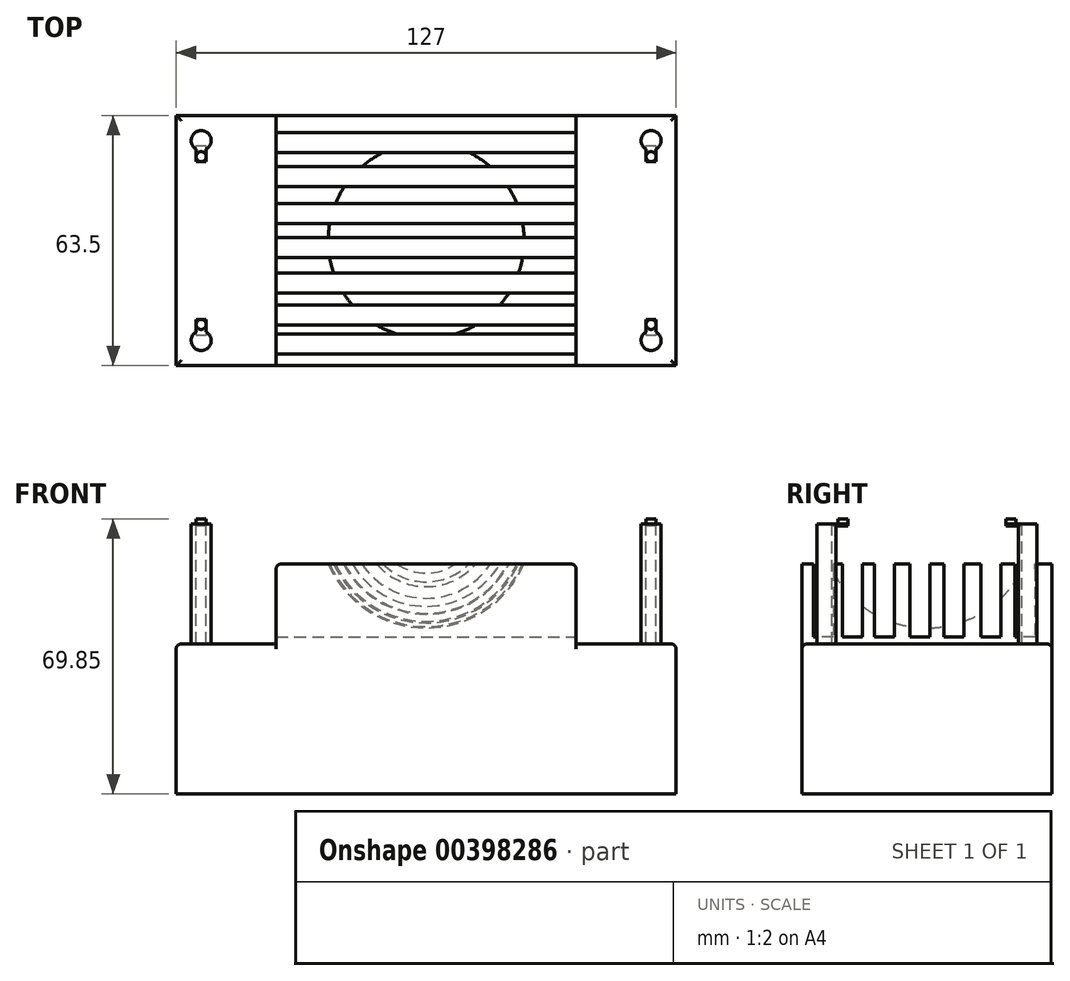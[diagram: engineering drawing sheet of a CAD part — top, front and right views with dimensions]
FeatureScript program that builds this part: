
annotation { "Feature Type Name" : "Feature", "Feature Type Description" : "" }
export const myFeature = defineFeature(function(context is Context, id is Id, definition is map)
    precondition{}
    {
        {
            var Q0;
            Q0=qCreatedBy(makeId("Top.planeOp"),FACE);
            var sketch = newSketch(context, id + "F0", { "sketchPlane" : qUnion([Q0])});
            skLineSegment(sketch, "E0.bottom", {"start": v(63.5, -31.75) * mm, "end": v(-63.5, -31.75) * mm});
            skLineSegment(sketch, "E0.top", {"start": v(63.5, 31.75) * mm, "end": v(-63.5, 31.75) * mm});
            skLineSegment(sketch, "E0.left", {"start": v(63.5, -31.75) * mm, "end": v(63.5, 31.75) * mm});
            skLineSegment(sketch, "E0.right", {"start": v(-63.5, -31.75) * mm, "end": v(-63.5, 31.75) * mm});
            skPoint(sketch, "E0.middle", {"position": v(0, 0) * mm});
            skSolve(sketch);
        }
        {
            var Q0;
            Q0=makeQuery(id+"F0.imprint","IMPRINT",FACE,{"disambiguationData":[TD([[makeQuery(id+"F0.imprint","IMPRINT",EDGE,{"derivedFrom":sQuery(id+"F0.wireOp",EDGE,"E0.bottom")}),-1.0]])]});
            extrude(context, id + "F1", {"entities" : qUnion([Q0]), "depth" : 38.1 * mm});
        }
        {
            var Q0;
            Q0=makeQuery(id+"F1.opExtrude","CAP_FACE",FACE,{"disambiguationData":[OSD([sQuery(id+"F0.wireOp",EDGE,"E0.bottom"),sQuery(id+"F0.wireOp",EDGE,"E0.top"),sQuery(id+"F0.wireOp",EDGE,"E0.left"),sQuery(id+"F0.wireOp",EDGE,"E0.right")])],"isStart":false});
            var sketch = newSketch(context, id + "F2", { "sketchPlane" : qUnion([Q0])});
            skLineSegment(sketch, "E1.bottom", {"start": v(-38.1, 31.75) * mm, "end": v(38.1, 31.75) * mm});
            skLineSegment(sketch, "E1.top", {"start": v(-38.1, -31.75) * mm, "end": v(38.1, -31.75) * mm});
            skLineSegment(sketch, "E1.left", {"start": v(-38.1, 31.75) * mm, "end": v(-38.1, -31.75) * mm});
            skLineSegment(sketch, "E1.right", {"start": v(38.1, 31.75) * mm, "end": v(38.1, -31.75) * mm});
            skSolve(sketch);
        }
        {
            var Q0;
            Q0=makeQuery(id+"F2.imprint","IMPRINT",FACE,{"disambiguationData":[TD([[makeQuery(id+"F2.imprint","IMPRINT",EDGE,{"derivedFrom":sQuery(id+"F2.wireOp",EDGE,"E1.bottom")}),1.0]])]});
            extrude(context, id + "F3", {"entities" : qUnion([Q0]), "operationType" : NewBodyOperationType.ADD, "depth" : 20.32 * mm});
        }
        {
            var Q0;
            Q0=qCreatedBy(makeId("Top.planeOp"),FACE);
            cPlane(context, id + "F4", {"entities" : qUnion([Q0]), "cplaneType" : CPlaneType.OFFSET, "offset" : 74.68 * mm, "width" : 152.4 * mm, "height" : 152.4 * mm});
        }
        {
            var Q0;
            Q0=qCreatedBy(id+"F4.planeOp",FACE);
            var sketch = newSketch(context, id + "F5", { "sketchPlane" : qUnion([Q0])});
            skLineSegment(sketch, "E2.bottom", {"start": v(-41.41, 27.43) * mm, "end": v(44.52, 27.43) * mm});
            skLineSegment(sketch, "E2.top", {"start": v(-41.41, 22.35) * mm, "end": v(44.52, 22.35) * mm});
            skLineSegment(sketch, "E2.left", {"start": v(-41.41, 27.43) * mm, "end": v(-41.41, 22.35) * mm});
            skLineSegment(sketch, "E2.right", {"start": v(44.52, 27.43) * mm, "end": v(44.52, 22.35) * mm});
            skLineSegment(sketch, "E3.bottom", {"start": v(-41.03, 18.8) * mm, "end": v(44.9, 18.8) * mm});
            skLineSegment(sketch, "E3.top", {"start": v(-41.03, 13.72) * mm, "end": v(44.9, 13.72) * mm});
            skLineSegment(sketch, "E3.left", {"start": v(-41.03, 18.8) * mm, "end": v(-41.03, 13.72) * mm});
            skLineSegment(sketch, "E3.right", {"start": v(44.9, 18.8) * mm, "end": v(44.9, 13.72) * mm});
            skLineSegment(sketch, "E4.bottom", {"start": v(-41, 9.4) * mm, "end": v(44.94, 9.4) * mm});
            skLineSegment(sketch, "E4.top", {"start": v(-41, 4.32) * mm, "end": v(44.94, 4.32) * mm});
            skLineSegment(sketch, "E4.left", {"start": v(-41, 9.4) * mm, "end": v(-41, 4.32) * mm});
            skLineSegment(sketch, "E4.right", {"start": v(44.94, 9.4) * mm, "end": v(44.94, 4.32) * mm});
            skLineSegment(sketch, "E5.bottom", {"start": v(-40.8, 0.73) * mm, "end": v(45.13, 0.73) * mm});
            skLineSegment(sketch, "E5.top", {"start": v(-40.8, -4.35) * mm, "end": v(45.13, -4.35) * mm});
            skLineSegment(sketch, "E5.left", {"start": v(-40.8, 0.73) * mm, "end": v(-40.8, -4.35) * mm});
            skLineSegment(sketch, "E5.right", {"start": v(45.13, 0.73) * mm, "end": v(45.13, -4.35) * mm});
            skLineSegment(sketch, "E6.bottom", {"start": v(-40.2, -8.25) * mm, "end": v(45.73, -8.25) * mm});
            skLineSegment(sketch, "E6.top", {"start": v(-40.2, -13.33) * mm, "end": v(45.73, -13.33) * mm});
            skLineSegment(sketch, "E6.left", {"start": v(-40.2, -8.25) * mm, "end": v(-40.2, -13.33) * mm});
            skLineSegment(sketch, "E6.right", {"start": v(45.73, -8.25) * mm, "end": v(45.73, -13.33) * mm});
            skLineSegment(sketch, "E7.bottom", {"start": v(-40.68, -16.38) * mm, "end": v(45.25, -16.38) * mm});
            skLineSegment(sketch, "E7.top", {"start": v(-40.68, -21.46) * mm, "end": v(45.25, -21.46) * mm});
            skLineSegment(sketch, "E7.left", {"start": v(-40.68, -16.38) * mm, "end": v(-40.68, -21.46) * mm});
            skLineSegment(sketch, "E7.right", {"start": v(45.25, -16.38) * mm, "end": v(45.25, -21.46) * mm});
            skLineSegment(sketch, "E8.bottom", {"start": v(-40.56, -23.75) * mm, "end": v(45.38, -23.75) * mm});
            skLineSegment(sketch, "E8.top", {"start": v(-40.56, -28.83) * mm, "end": v(45.38, -28.83) * mm});
            skLineSegment(sketch, "E8.left", {"start": v(-40.56, -23.75) * mm, "end": v(-40.56, -28.83) * mm});
            skLineSegment(sketch, "E8.right", {"start": v(45.38, -23.75) * mm, "end": v(45.38, -28.83) * mm});
            skSolve(sketch);
        }
        {
            var Q0;
            Q0 = qSketchRegion(id + "F5", true);
            extrude(context, id + "F6", {"entities" : qUnion([Q0]), "operationType" : NewBodyOperationType.REMOVE, "oppositeDirection" : true, "depth" : 34.8 * mm});
        }
        {
            var Q0;
            Q0=makeQuery(id+"F1.opExtrude","CAP_EDGE",EDGE,{"disambiguationData":[OSD([sQuery(id+"F0.wireOp",EDGE,"E0.right")])],"isStart":false});
            var Q1;
            {var subQ0=sQuery(id+"F0.wireOp",EDGE,"E0.right");var subQ1=sQuery(id+"F0.wireOp",EDGE,"E0.bottom");Q1=makeQuery(id+"F3.boolean.opBoolean","SPLIT",EDGE,{"disambiguationData":[TD([makeQuery(id+"F1.opExtrude","SWEPT_FACE",FACE,{"disambiguationData":[OSD([subQ0])]})])],"derivedFrom":makeQuery(id+"F1.opExtrude","CAP_EDGE",EDGE,{"disambiguationData":[OSD([subQ1])],"isStart":false})});}
            var Q2;
            {var subQ0=sQuery(id+"F2.wireOp",EDGE,"E1.left");Q2=makeQuery(id+"F6.boolean.opBoolean","SPLIT",EDGE,{"disambiguationData":[TD([makeQuery(id+"F6.opExtrude","SWEPT_FACE",FACE,{"disambiguationData":[OSD([sQuery(id+"F5.wireOp",EDGE,"E5.top")])]})])],"derivedFrom":makeQuery(id+"F3.opExtrude","CAP_EDGE",EDGE,{"disambiguationData":[OSD([subQ0])],"isStart":false})});}
            var Q3;
            {var subQ0=sQuery(id+"F2.wireOp",EDGE,"E1.left");Q3=makeQuery(id+"F6.boolean.opBoolean","SPLIT",EDGE,{"disambiguationData":[TD([makeQuery(id+"F6.opExtrude","SWEPT_FACE",FACE,{"disambiguationData":[OSD([sQuery(id+"F5.wireOp",EDGE,"E6.top")])]})])],"derivedFrom":makeQuery(id+"F3.opExtrude","CAP_EDGE",EDGE,{"disambiguationData":[OSD([subQ0])],"isStart":false})});}
            var Q4;
            {var subQ0=sQuery(id+"F2.wireOp",EDGE,"E1.left");Q4=makeQuery(id+"F6.boolean.opBoolean","SPLIT",EDGE,{"disambiguationData":[TD([makeQuery(id+"F1.opExtrude","SWEPT_FACE",FACE,{"disambiguationData":[OSD([sQuery(id+"F0.wireOp",EDGE,"E0.bottom")])]})])],"derivedFrom":makeQuery(id+"F3.opExtrude","CAP_EDGE",EDGE,{"disambiguationData":[OSD([subQ0])],"isStart":false})});}
            var Q5;
            {var subQ0=sQuery(id+"F2.wireOp",EDGE,"E1.left");Q5=makeQuery(id+"F6.boolean.opBoolean","SPLIT",EDGE,{"disambiguationData":[TD([makeQuery(id+"F6.opExtrude","SWEPT_FACE",FACE,{"disambiguationData":[OSD([sQuery(id+"F5.wireOp",EDGE,"E7.top")])]})])],"derivedFrom":makeQuery(id+"F3.opExtrude","CAP_EDGE",EDGE,{"disambiguationData":[OSD([subQ0])],"isStart":false})});}
            var Q6;
            {var subQ0=sQuery(id+"F2.wireOp",EDGE,"E1.left");Q6=makeQuery(id+"F6.boolean.opBoolean","SPLIT",EDGE,{"disambiguationData":[TD([makeQuery(id+"F6.opExtrude","SWEPT_FACE",FACE,{"disambiguationData":[OSD([sQuery(id+"F5.wireOp",EDGE,"E3.top")])]})])],"derivedFrom":makeQuery(id+"F3.opExtrude","CAP_EDGE",EDGE,{"disambiguationData":[OSD([subQ0])],"isStart":false})});}
            var Q7;
            {var subQ0=sQuery(id+"F2.wireOp",EDGE,"E1.left");Q7=makeQuery(id+"F6.boolean.opBoolean","SPLIT",EDGE,{"disambiguationData":[TD([makeQuery(id+"F6.opExtrude","SWEPT_FACE",FACE,{"disambiguationData":[OSD([sQuery(id+"F5.wireOp",EDGE,"E2.top")])]})])],"derivedFrom":makeQuery(id+"F3.opExtrude","CAP_EDGE",EDGE,{"disambiguationData":[OSD([subQ0])],"isStart":false})});}
            var Q8;
            {var subQ0=sQuery(id+"F2.wireOp",EDGE,"E1.left");Q8=makeQuery(id+"F6.boolean.opBoolean","SPLIT",EDGE,{"disambiguationData":[TD([makeQuery(id+"F1.opExtrude","SWEPT_FACE",FACE,{"disambiguationData":[OSD([sQuery(id+"F0.wireOp",EDGE,"E0.top")])]})])],"derivedFrom":makeQuery(id+"F3.opExtrude","CAP_EDGE",EDGE,{"disambiguationData":[OSD([subQ0])],"isStart":false})});}
            var Q9;
            {var subQ0=sQuery(id+"F2.wireOp",EDGE,"E1.left");Q9=makeQuery(id+"F6.boolean.opBoolean","SPLIT",EDGE,{"disambiguationData":[TD([makeQuery(id+"F6.opExtrude","SWEPT_FACE",FACE,{"disambiguationData":[OSD([sQuery(id+"F5.wireOp",EDGE,"E4.top")])]})])],"derivedFrom":makeQuery(id+"F3.opExtrude","CAP_EDGE",EDGE,{"disambiguationData":[OSD([subQ0])],"isStart":false})});}
            var Q10;
            {var subQ0=sQuery(id+"F0.wireOp",EDGE,"E0.right");var subQ1=sQuery(id+"F0.wireOp",EDGE,"E0.top");Q10=makeQuery(id+"F3.boolean.opBoolean","SPLIT",EDGE,{"disambiguationData":[TD([makeQuery(id+"F1.opExtrude","SWEPT_FACE",FACE,{"disambiguationData":[OSD([subQ0])]})])],"derivedFrom":makeQuery(id+"F1.opExtrude","CAP_EDGE",EDGE,{"disambiguationData":[OSD([subQ1])],"isStart":false})});}
            var Q11;
            Q11=makeQuery(id+"F1.opExtrude","CAP_EDGE",EDGE,{"disambiguationData":[OSD([sQuery(id+"F0.wireOp",EDGE,"E0.left")])],"isStart":false});
            var Q12;
            {var subQ0=sQuery(id+"F0.wireOp",EDGE,"E0.left");var subQ1=sQuery(id+"F0.wireOp",EDGE,"E0.top");Q12=makeQuery(id+"F3.boolean.opBoolean","SPLIT",EDGE,{"disambiguationData":[TD([makeQuery(id+"F1.opExtrude","SWEPT_FACE",FACE,{"disambiguationData":[OSD([subQ0])]})])],"derivedFrom":makeQuery(id+"F1.opExtrude","CAP_EDGE",EDGE,{"disambiguationData":[OSD([subQ1])],"isStart":false})});}
            var Q13;
            {var subQ0=sQuery(id+"F0.wireOp",EDGE,"E0.left");var subQ1=sQuery(id+"F0.wireOp",EDGE,"E0.bottom");Q13=makeQuery(id+"F3.boolean.opBoolean","SPLIT",EDGE,{"disambiguationData":[TD([makeQuery(id+"F1.opExtrude","SWEPT_FACE",FACE,{"disambiguationData":[OSD([subQ0])]})])],"derivedFrom":makeQuery(id+"F1.opExtrude","CAP_EDGE",EDGE,{"disambiguationData":[OSD([subQ1])],"isStart":false})});}
            var Q14;
            {var subQ0=sQuery(id+"F2.wireOp",EDGE,"E1.right");Q14=makeQuery(id+"F6.boolean.opBoolean","SPLIT",EDGE,{"disambiguationData":[TD([makeQuery(id+"F6.opExtrude","SWEPT_FACE",FACE,{"disambiguationData":[OSD([sQuery(id+"F5.wireOp",EDGE,"E4.top")])]})])],"derivedFrom":makeQuery(id+"F3.opExtrude","CAP_EDGE",EDGE,{"disambiguationData":[OSD([subQ0])],"isStart":false})});}
            var Q15;
            {var subQ0=sQuery(id+"F2.wireOp",EDGE,"E1.right");Q15=makeQuery(id+"F6.boolean.opBoolean","SPLIT",EDGE,{"disambiguationData":[TD([makeQuery(id+"F6.opExtrude","SWEPT_FACE",FACE,{"disambiguationData":[OSD([sQuery(id+"F5.wireOp",EDGE,"E3.top")])]})])],"derivedFrom":makeQuery(id+"F3.opExtrude","CAP_EDGE",EDGE,{"disambiguationData":[OSD([subQ0])],"isStart":false})});}
            var Q16;
            {var subQ0=sQuery(id+"F2.wireOp",EDGE,"E1.right");Q16=makeQuery(id+"F6.boolean.opBoolean","SPLIT",EDGE,{"disambiguationData":[TD([makeQuery(id+"F6.opExtrude","SWEPT_FACE",FACE,{"disambiguationData":[OSD([sQuery(id+"F5.wireOp",EDGE,"E2.top")])]})])],"derivedFrom":makeQuery(id+"F3.opExtrude","CAP_EDGE",EDGE,{"disambiguationData":[OSD([subQ0])],"isStart":false})});}
            var Q17;
            {var subQ0=sQuery(id+"F2.wireOp",EDGE,"E1.right");Q17=makeQuery(id+"F6.boolean.opBoolean","SPLIT",EDGE,{"disambiguationData":[TD([makeQuery(id+"F1.opExtrude","SWEPT_FACE",FACE,{"disambiguationData":[OSD([sQuery(id+"F0.wireOp",EDGE,"E0.top")])]})])],"derivedFrom":makeQuery(id+"F3.opExtrude","CAP_EDGE",EDGE,{"disambiguationData":[OSD([subQ0])],"isStart":false})});}
            var Q18;
            {var subQ0=sQuery(id+"F2.wireOp",EDGE,"E1.right");Q18=makeQuery(id+"F6.boolean.opBoolean","SPLIT",EDGE,{"disambiguationData":[TD([makeQuery(id+"F6.opExtrude","SWEPT_FACE",FACE,{"disambiguationData":[OSD([sQuery(id+"F5.wireOp",EDGE,"E5.top")])]})])],"derivedFrom":makeQuery(id+"F3.opExtrude","CAP_EDGE",EDGE,{"disambiguationData":[OSD([subQ0])],"isStart":false})});}
            var Q19;
            {var subQ0=sQuery(id+"F2.wireOp",EDGE,"E1.right");Q19=makeQuery(id+"F6.boolean.opBoolean","SPLIT",EDGE,{"disambiguationData":[TD([makeQuery(id+"F6.opExtrude","SWEPT_FACE",FACE,{"disambiguationData":[OSD([sQuery(id+"F5.wireOp",EDGE,"E6.top")])]})])],"derivedFrom":makeQuery(id+"F3.opExtrude","CAP_EDGE",EDGE,{"disambiguationData":[OSD([subQ0])],"isStart":false})});}
            var Q20;
            {var subQ0=sQuery(id+"F2.wireOp",EDGE,"E1.right");Q20=makeQuery(id+"F6.boolean.opBoolean","SPLIT",EDGE,{"disambiguationData":[TD([makeQuery(id+"F6.opExtrude","SWEPT_FACE",FACE,{"disambiguationData":[OSD([sQuery(id+"F5.wireOp",EDGE,"E7.top")])]})])],"derivedFrom":makeQuery(id+"F3.opExtrude","CAP_EDGE",EDGE,{"disambiguationData":[OSD([subQ0])],"isStart":false})});}
            var Q21;
            {var subQ0=sQuery(id+"F2.wireOp",EDGE,"E1.right");Q21=makeQuery(id+"F6.boolean.opBoolean","SPLIT",EDGE,{"disambiguationData":[TD([makeQuery(id+"F1.opExtrude","SWEPT_FACE",FACE,{"disambiguationData":[OSD([sQuery(id+"F0.wireOp",EDGE,"E0.bottom")])]})])],"derivedFrom":makeQuery(id+"F3.opExtrude","CAP_EDGE",EDGE,{"disambiguationData":[OSD([subQ0])],"isStart":false})});}
            fillet(context, id + "F7", {"entities" : qUnion([Q0, Q1, Q2, Q3, Q4, Q5, Q6, Q7, Q8, Q9, Q10, Q11, Q12, Q13, Q14, Q15, Q16, Q17, Q18, Q19, Q20, Q21]), "radius" : 1.27 * mm, "tangentPropagation" : true, "allowEdgeOverflow" : false});
        }
        {
            var Q0;
            Q0=qCreatedBy(makeId("Top.planeOp"),FACE);
            cPlane(context, id + "F8", {"entities" : qUnion([Q0]), "cplaneType" : CPlaneType.OFFSET, "offset" : 69.34 * mm, "width" : 152.4 * mm, "height" : 152.4 * mm});
        }
        {
            var Q0;
            Q0=qCreatedBy(id+"F8.planeOp",FACE);
            var sketch = newSketch(context, id + "F9", { "sketchPlane" : qUnion([Q0])});
            skCircle(sketch, "E9", {"center": v(0, 0) * mm, "radius": 27.18 * mm});
            skLineSegment(sketch, "E10", {"start": v(0, 27.18) * mm, "end": v(0, -27.18) * mm});
            skSolve(sketch);
        }
        {
            var Q0;
            Q0=qCreatedBy(id+"F8.planeOp",FACE);
            var sketch = newSketch(context, id + "F10", { "sketchPlane" : qUnion([Q0])});
            skLineSegment(sketch, "E11", {"start": v(0, 27.11) * mm, "end": v(0, -26.67) * mm});
            skSolve(sketch);
        }
        {
            var Q0;
            {var subQ0=sQuery(id+"F9.wireOp",EDGE,"E10");Q0=makeQuery(id+"F9.imprint","IMPRINT",FACE,{"disambiguationData":[TD([[makeQuery(id+"F9.imprint","IMPRINT",EDGE,{"derivedFrom":subQ0}),-1.0]])]});}
            var Q1;
            Q1=sQuery(id+"F10.wireOp",EDGE,"E11");
            revolve(context, id + "F11", {"operationType" : NewBodyOperationType.REMOVE, "entities" : qUnion([Q0]), "axis" : qUnion([Q1]), "revolveType" : RevolveType.FULL, "oppositeDirection" : true});
        }
        {
            var Q0;
            {var subQ0=sQuery(id+"F0.wireOp",EDGE,"E0.left");var subQ1=sQuery(id+"F0.wireOp",EDGE,"E0.top");var subQ2=sQuery(id+"F0.wireOp",EDGE,"E0.bottom");Q0=makeQuery(id+"F3.boolean.opBoolean","SPLIT",FACE,{"disambiguationData":[TD([makeQuery(id+"F1.opExtrude","SWEPT_FACE",FACE,{"disambiguationData":[OSD([subQ0])]})])],"derivedFrom":makeQuery(id+"F1.opExtrude","CAP_FACE",FACE,{"disambiguationData":[OSD([subQ2,subQ1,subQ0,sQuery(id+"F0.wireOp",EDGE,"E0.right")])],"isStart":false})});}
            var sketch = newSketch(context, id + "F12", { "sketchPlane" : qUnion([Q0])});
            skCircle(sketch, "E12", {"center": v(-57.15, 25.4) * mm, "radius": 2.54 * mm});
            skCircle(sketch, "E13", {"center": v(-57.15, -25.4) * mm, "radius": 2.54 * mm});
            skSolve(sketch);
        }
        {
            var Q0;
            Q0=makeQuery(id+"F12.imprint","IMPRINT",FACE,{"disambiguationData":[TD([[makeQuery(id+"F12.imprint","IMPRINT",EDGE,{"derivedFrom":sQuery(id+"F12.wireOp",EDGE,"E12")}),1.0]])]});
            var Q1;
            Q1=makeQuery(id+"F12.imprint","IMPRINT",FACE,{"disambiguationData":[TD([[makeQuery(id+"F12.imprint","IMPRINT",EDGE,{"derivedFrom":sQuery(id+"F12.wireOp",EDGE,"E13")}),1.0]])]});
            extrude(context, id + "F13", {"entities" : qUnion([Q0, Q1]), "operationType" : NewBodyOperationType.ADD, "depth" : 30.48 * mm});
        }
        {
            var Q0;
            {var subQ0=sQuery(id+"F0.wireOp",EDGE,"E0.left");var subQ1=sQuery(id+"F0.wireOp",EDGE,"E0.top");var subQ2=sQuery(id+"F0.wireOp",EDGE,"E0.bottom");Q0=makeQuery(id+"F3.boolean.opBoolean","SPLIT",FACE,{"disambiguationData":[TD([makeQuery(id+"F1.opExtrude","SWEPT_FACE",FACE,{"disambiguationData":[OSD([subQ0])]})])],"derivedFrom":makeQuery(id+"F1.opExtrude","CAP_FACE",FACE,{"disambiguationData":[OSD([subQ2,subQ1,subQ0,sQuery(id+"F0.wireOp",EDGE,"E0.right")])],"isStart":false})});}
            var sketch = newSketch(context, id + "F14", { "sketchPlane" : qUnion([Q0])});
            skCircle(sketch, "E14", {"center": v(57.15, 25.4) * mm, "radius": 2.54 * mm});
            skCircle(sketch, "E15", {"center": v(57.15, -25.4) * mm, "radius": 2.54 * mm});
            skSolve(sketch);
        }
        {
            var Q0;
            Q0=makeQuery(id+"F14.imprint","IMPRINT",FACE,{"disambiguationData":[TD([[makeQuery(id+"F14.imprint","IMPRINT",EDGE,{"derivedFrom":sQuery(id+"F14.wireOp",EDGE,"E14")}),1.0]])]});
            var Q1;
            Q1=makeQuery(id+"F14.imprint","IMPRINT",FACE,{"disambiguationData":[TD([[makeQuery(id+"F14.imprint","IMPRINT",EDGE,{"derivedFrom":sQuery(id+"F14.wireOp",EDGE,"E15")}),1.0]])]});
            extrude(context, id + "F15", {"entities" : qUnion([Q0, Q1]), "operationType" : NewBodyOperationType.ADD, "depth" : 30.48 * mm});
        }
        {
            var Q0;
            Q0=qCreatedBy(makeId("Top.planeOp"),FACE);
            cPlane(context, id + "F16", {"entities" : qUnion([Q0]), "cplaneType" : CPlaneType.OFFSET, "offset" : 68.83 * mm, "width" : 152.4 * mm, "height" : 152.4 * mm});
        }
        {
            var Q0;
            Q0=qCreatedBy(id+"F16.planeOp",FACE);
            var sketch = newSketch(context, id + "F17", { "sketchPlane" : qUnion([Q0])});
            skLineSegment(sketch, "E16.bottom", {"start": v(-58.42, 24.13) * mm, "end": v(-55.88, 24.13) * mm});
            skLineSegment(sketch, "E16.top", {"start": v(-58.42, -24.13) * mm, "end": v(-55.88, -24.13) * mm});
            skLineSegment(sketch, "E16.left", {"start": v(-58.42, 24.13) * mm, "end": v(-58.42, -24.13) * mm});
            skLineSegment(sketch, "E16.right", {"start": v(-55.88, 24.13) * mm, "end": v(-55.88, -24.13) * mm});
            skLineSegment(sketch, "E17.bottom", {"start": v(55.88, 24.13) * mm, "end": v(58.42, 24.13) * mm});
            skLineSegment(sketch, "E17.top", {"start": v(55.88, -24.13) * mm, "end": v(58.42, -24.13) * mm});
            skLineSegment(sketch, "E17.left", {"start": v(55.88, 24.13) * mm, "end": v(55.88, -24.13) * mm});
            skLineSegment(sketch, "E17.right", {"start": v(58.42, 24.13) * mm, "end": v(58.42, -24.13) * mm});
            skSolve(sketch);
        }
        {
            var Q0;
            Q0 = qSketchRegion(id + "F17", true);
            extrude(context, id + "F18", {"entities" : qUnion([Q0]), "operationType" : NewBodyOperationType.REMOVE, "oppositeDirection" : true, "depth" : 30.73 * mm});
        }
        {
            var Q0;
            Q0=makeQuery(id+"F18.boolean.opBoolean","COPY",FACE,{"derivedFrom":makeQuery(id+"F18.opExtrude","SWEPT_FACE",FACE,{"disambiguationData":[OSD([sQuery(id+"F17.wireOp",EDGE,"E16.bottom")])]})});
            var sketch = newSketch(context, id + "F19", { "sketchPlane" : qUnion([Q0])});
            skLineSegment(sketch, "E18.bottom", {"start": v(-58.42, 68.58) * mm, "end": v(-55.88, 68.58) * mm});
            skLineSegment(sketch, "E18.top", {"start": v(-58.42, 68.07) * mm, "end": v(-55.88, 68.07) * mm});
            skLineSegment(sketch, "E18.left", {"start": v(-58.42, 68.58) * mm, "end": v(-58.42, 68.07) * mm});
            skLineSegment(sketch, "E18.right", {"start": v(-55.88, 68.58) * mm, "end": v(-55.88, 68.07) * mm});
            skSolve(sketch);
        }
        {
            var Q0;
            Q0 = qSketchRegion(id + "F19", true);
            extrude(context, id + "F20", {"entities" : qUnion([Q0]), "operationType" : NewBodyOperationType.ADD, "depth" : 4.1 * mm});
        }
        {
            var Q0;
            Q0=makeQuery(id+"F20.boolean.opBoolean","MERGE",FACE,{"derivedFrom":[makeQuery(id+"F13.opExtrude","CAP_FACE",FACE,{"disambiguationData":[OSD([sQuery(id+"F12.wireOp",EDGE,"E12")])],"isStart":false}),makeQuery(id+"F20.opExtrude","SWEPT_FACE",FACE,{"disambiguationData":[OSD([sQuery(id+"F19.wireOp",EDGE,"E18.bottom")])]})]});
            var sketch = newSketch(context, id + "F21", { "sketchPlane" : qUnion([Q0])});
            skCircle(sketch, "E19", {"center": v(-57.15, 21.31) * mm, "radius": 1.27 * mm});
            skSolve(sketch);
        }
        {
            var Q0;
            Q0 = qSketchRegion(id + "F21", true);
            extrude(context, id + "F22", {"entities" : qUnion([Q0]), "operationType" : NewBodyOperationType.ADD, "depth" : 1.27 * mm});
        }
        {
            var Q0;
            Q0=makeQuery(id+"F18.boolean.opBoolean","COPY",FACE,{"derivedFrom":makeQuery(id+"F18.opExtrude","SWEPT_FACE",FACE,{"disambiguationData":[OSD([sQuery(id+"F17.wireOp",EDGE,"E16.top")])]})});
            var sketch = newSketch(context, id + "F23", { "sketchPlane" : qUnion([Q0])});
            skLineSegment(sketch, "E20.bottom", {"start": v(55.88, 68.58) * mm, "end": v(58.42, 68.58) * mm});
            skLineSegment(sketch, "E20.top", {"start": v(55.88, 68.07) * mm, "end": v(58.42, 68.07) * mm});
            skLineSegment(sketch, "E20.left", {"start": v(55.88, 68.58) * mm, "end": v(55.88, 68.07) * mm});
            skLineSegment(sketch, "E20.right", {"start": v(58.42, 68.58) * mm, "end": v(58.42, 68.07) * mm});
            skSolve(sketch);
        }
        {
            var Q0;
            Q0 = qSketchRegion(id + "F23", true);
            extrude(context, id + "F24", {"entities" : qUnion([Q0]), "operationType" : NewBodyOperationType.ADD, "depth" : 4.1 * mm});
        }
        {
            var Q0;
            Q0=makeQuery(id+"F24.boolean.opBoolean","MERGE",FACE,{"derivedFrom":[makeQuery(id+"F13.opExtrude","CAP_FACE",FACE,{"disambiguationData":[OSD([sQuery(id+"F12.wireOp",EDGE,"E13")])],"isStart":false}),makeQuery(id+"F24.opExtrude","SWEPT_FACE",FACE,{"disambiguationData":[OSD([sQuery(id+"F23.wireOp",EDGE,"E20.bottom")])]})]});
            var sketch = newSketch(context, id + "F25", { "sketchPlane" : qUnion([Q0])});
            skCircle(sketch, "E21", {"center": v(-57.15, -21.31) * mm, "radius": 1.27 * mm});
            skSolve(sketch);
        }
        {
            var Q0;
            {var subQ0=sQuery(id+"F25.wireOp",EDGE,"E21");var subQ1=sQuery(id+"F23.wireOp",EDGE,"E20.bottom");var subQ2=makeQuery(id+"F25.imprint","INTERSECT",VERTEX,{"derivedFrom":[makeQuery(id+"F24.opExtrude","CAP_EDGE",EDGE,{"disambiguationData":[OSD([subQ1])],"isStart":false}),subQ0]});Q0=makeQuery(id+"F25.imprint","IMPRINT",FACE,{"disambiguationData":[TD([[makeQuery(id+"F25.imprint","IMPRINT",EDGE,{"disambiguationData":[TD([[subQ2,1.0]])],"derivedFrom":subQ0}),1.0]])]});}
            extrude(context, id + "F26", {"entities" : qUnion([Q0]), "operationType" : NewBodyOperationType.ADD, "depth" : 1.27 * mm});
        }
        {
            var Q0;
            Q0=makeQuery(id+"F18.boolean.opBoolean","COPY",FACE,{"derivedFrom":makeQuery(id+"F18.opExtrude","SWEPT_FACE",FACE,{"disambiguationData":[OSD([sQuery(id+"F17.wireOp",EDGE,"E17.bottom")])]})});
            var sketch = newSketch(context, id + "F27", { "sketchPlane" : qUnion([Q0])});
            skLineSegment(sketch, "E22.bottom", {"start": v(55.88, 68.58) * mm, "end": v(58.42, 68.58) * mm});
            skLineSegment(sketch, "E22.top", {"start": v(55.88, 68.07) * mm, "end": v(58.42, 68.07) * mm});
            skLineSegment(sketch, "E22.left", {"start": v(55.88, 68.58) * mm, "end": v(55.88, 68.07) * mm});
            skLineSegment(sketch, "E22.right", {"start": v(58.42, 68.58) * mm, "end": v(58.42, 68.07) * mm});
            skSolve(sketch);
        }
        {
            var Q0;
            Q0 = qSketchRegion(id + "F27", true);
            extrude(context, id + "F28", {"entities" : qUnion([Q0]), "operationType" : NewBodyOperationType.ADD, "depth" : 4.1 * mm});
        }
        {
            var Q0;
            Q0=makeQuery(id+"F28.boolean.opBoolean","MERGE",FACE,{"derivedFrom":[makeQuery(id+"F15.opExtrude","CAP_FACE",FACE,{"disambiguationData":[OSD([sQuery(id+"F14.wireOp",EDGE,"E14")])],"isStart":false}),makeQuery(id+"F28.opExtrude","SWEPT_FACE",FACE,{"disambiguationData":[OSD([sQuery(id+"F27.wireOp",EDGE,"E22.bottom")])]})]});
            var sketch = newSketch(context, id + "F29", { "sketchPlane" : qUnion([Q0])});
            skCircle(sketch, "E23", {"center": v(57.15, 21.31) * mm, "radius": 1.27 * mm});
            skSolve(sketch);
        }
        {
            var Q0;
            Q0 = qSketchRegion(id + "F29", true);
            extrude(context, id + "F30", {"entities" : qUnion([Q0]), "operationType" : NewBodyOperationType.ADD, "depth" : 1.27 * mm});
        }
        {
            var Q0;
            Q0=makeQuery(id+"F18.boolean.opBoolean","COPY",FACE,{"derivedFrom":makeQuery(id+"F18.opExtrude","SWEPT_FACE",FACE,{"disambiguationData":[OSD([sQuery(id+"F17.wireOp",EDGE,"E17.top")])]})});
            var sketch = newSketch(context, id + "F31", { "sketchPlane" : qUnion([Q0])});
            skLineSegment(sketch, "E24.bottom", {"start": v(-58.42, 68.58) * mm, "end": v(-55.88, 68.58) * mm});
            skLineSegment(sketch, "E24.top", {"start": v(-58.42, 68.07) * mm, "end": v(-55.88, 68.07) * mm});
            skLineSegment(sketch, "E24.left", {"start": v(-58.42, 68.58) * mm, "end": v(-58.42, 68.07) * mm});
            skLineSegment(sketch, "E24.right", {"start": v(-55.88, 68.58) * mm, "end": v(-55.88, 68.07) * mm});
            skSolve(sketch);
        }
        {
            var Q0;
            Q0 = qSketchRegion(id + "F31", true);
            extrude(context, id + "F32", {"entities" : qUnion([Q0]), "operationType" : NewBodyOperationType.ADD, "depth" : 4.1 * mm});
        }
        {
            var Q0;
            Q0=makeQuery(id+"F32.boolean.opBoolean","MERGE",FACE,{"derivedFrom":[makeQuery(id+"F15.opExtrude","CAP_FACE",FACE,{"disambiguationData":[OSD([sQuery(id+"F14.wireOp",EDGE,"E15")])],"isStart":false}),makeQuery(id+"F32.opExtrude","SWEPT_FACE",FACE,{"disambiguationData":[OSD([sQuery(id+"F31.wireOp",EDGE,"E24.bottom")])]})]});
            var sketch = newSketch(context, id + "F33", { "sketchPlane" : qUnion([Q0])});
            skCircle(sketch, "E25", {"center": v(57.15, -21.31) * mm, "radius": 1.27 * mm});
            skSolve(sketch);
        }
        {
            var Q0;
            Q0 = qSketchRegion(id + "F33", true);
            extrude(context, id + "F34", {"entities" : qUnion([Q0]), "operationType" : NewBodyOperationType.ADD, "depth" : 1.27 * mm});
        }
    });
